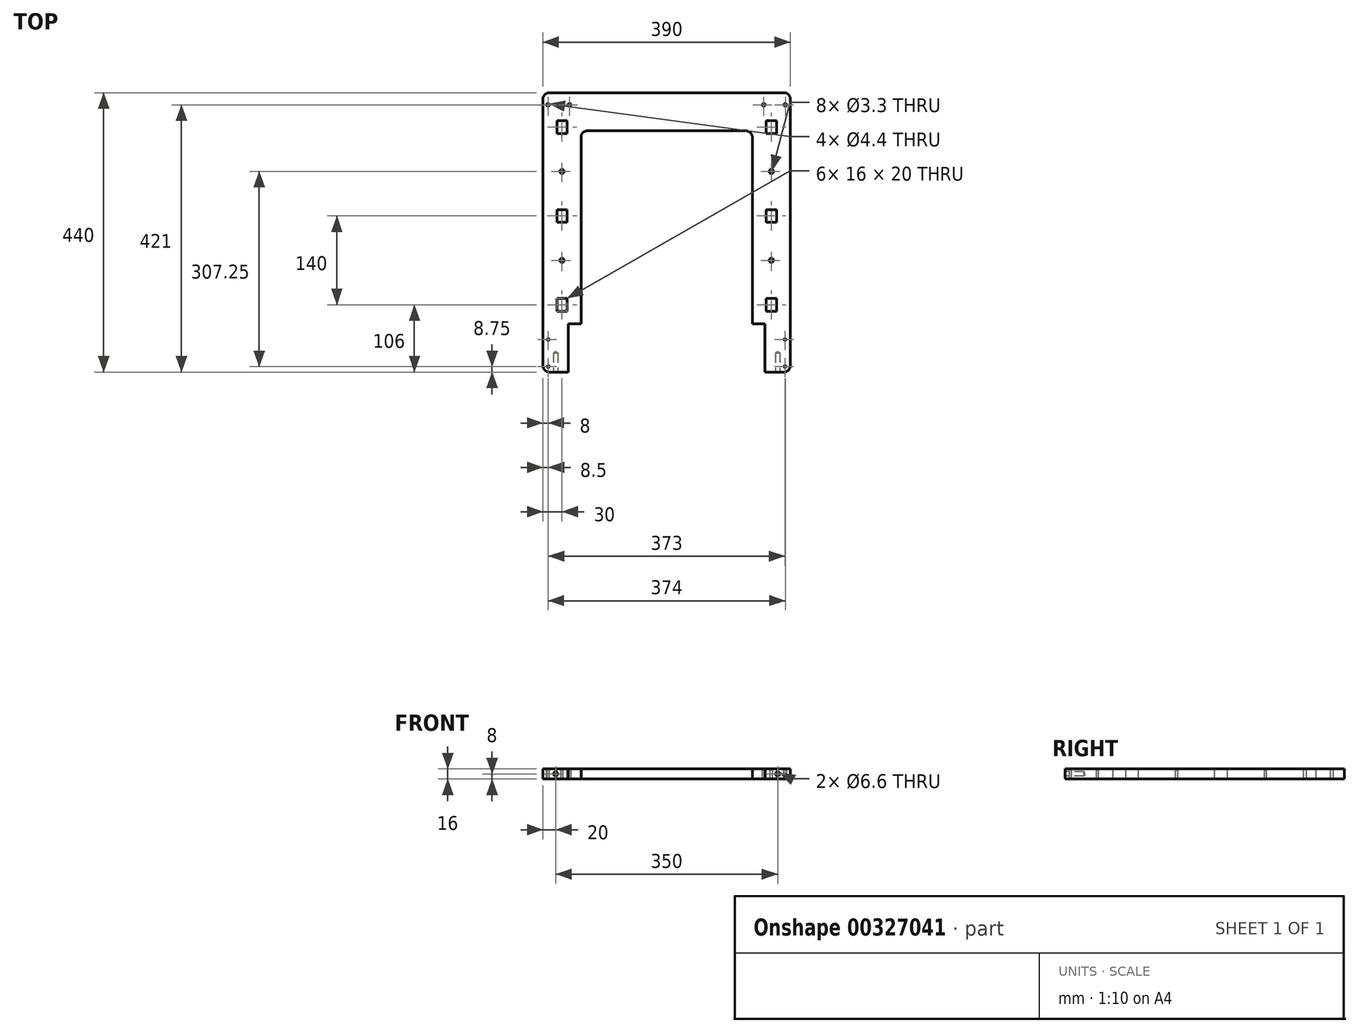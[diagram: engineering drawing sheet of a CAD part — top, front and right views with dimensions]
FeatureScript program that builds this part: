
annotation { "Feature Type Name" : "Feature", "Feature Type Description" : "" }
export const myFeature = defineFeature(function(context is Context, id is Id, definition is map)
    precondition{}
    {
        {
            var Q0;
            Q0=qCreatedBy(makeId("Top.planeOp"),FACE);
            var sketch = newSketch(context, id + "F0", { "sketchPlane" : qUnion([Q0])});
            skLineSegment(sketch, "E0.bottom", {"start": v(195, 220) * mm, "end": v(-195, 220) * mm});
            skLineSegment(sketch, "E0.top", {"start": v(195, -220) * mm, "end": v(-195, -220) * mm});
            skLineSegment(sketch, "E0.left", {"start": v(195, 220) * mm, "end": v(195, -220) * mm});
            skLineSegment(sketch, "E0.right", {"start": v(-195, 220) * mm, "end": v(-195, -220) * mm});
            skPoint(sketch, "E0.middle", {"position": v(0, 0) * mm});
            skLineSegment(sketch, "E1", {"start": v(-135, -220) * mm, "end": v(-135, 160) * mm});
            skLineSegment(sketch, "E2", {"start": v(-135, 160) * mm, "end": v(135, 160) * mm});
            skLineSegment(sketch, "E3", {"start": v(135, 160) * mm, "end": v(135, -220) * mm});
            skLineSegment(sketch, "E4", {"start": v(0, 0) * mm, "end": v(0, 160) * mm, "construction": true});
            skSolve(sketch);
        }
        {
            var Q0;
            Q0=makeQuery(id+"F0.imprint","IMPRINT",FACE,{"disambiguationData":[TD([[makeQuery(id+"F0.imprint","IMPRINT",EDGE,{"derivedFrom":sQuery(id+"F0.wireOp",EDGE,"E0.bottom")}),1.0]])]});
            extrude(context, id + "F1", {"entities" : qUnion([Q0]), "depth" : 16 * mm});
        }
        {
            var Q0;
            Q0=makeQuery(id+"F1.opExtrude","CAP_FACE",FACE,{"disambiguationData":[OSD([sQuery(id+"F0.wireOp",EDGE,"E0.bottom"),sQuery(id+"F0.wireOp",EDGE,"E0.top"),sQuery(id+"F0.wireOp",EDGE,"E0.left"),sQuery(id+"F0.wireOp",EDGE,"E0.right"),sQuery(id+"F0.wireOp",EDGE,"E1"),sQuery(id+"F0.wireOp",EDGE,"E2"),sQuery(id+"F0.wireOp",EDGE,"E3")])],"isStart":false});
            var sketch = newSketch(context, id + "F2", { "sketchPlane" : qUnion([Q0])});
            skLineSegment(sketch, "E5", {"start": v(-165, 166) * mm, "end": v(-165, 26) * mm, "construction": true});
            skLineSegment(sketch, "E6", {"start": v(-165, 26) * mm, "end": v(-165, -114) * mm, "construction": true});
            skLineSegment(sketch, "E7.bottom", {"start": v(-157, 176) * mm, "end": v(-173, 176) * mm});
            skLineSegment(sketch, "E7.top", {"start": v(-157, 156) * mm, "end": v(-173, 156) * mm});
            skLineSegment(sketch, "E7.left", {"start": v(-157, 176) * mm, "end": v(-157, 156) * mm});
            skLineSegment(sketch, "E7.right", {"start": v(-173, 176) * mm, "end": v(-173, 156) * mm});
            skPoint(sketch, "E7.middle", {"position": v(-165, 166) * mm});
            skLineSegment(sketch, "E8.bottom", {"start": v(-157, 36) * mm, "end": v(-173, 36) * mm});
            skLineSegment(sketch, "E8.top", {"start": v(-157, 16) * mm, "end": v(-173, 16) * mm});
            skLineSegment(sketch, "E8.left", {"start": v(-157, 36) * mm, "end": v(-157, 16) * mm});
            skLineSegment(sketch, "E8.right", {"start": v(-173, 36) * mm, "end": v(-173, 16) * mm});
            skPoint(sketch, "E8.middle", {"position": v(-165, 26) * mm});
            skLineSegment(sketch, "E9.bottom", {"start": v(-157, -104) * mm, "end": v(-173, -104) * mm});
            skLineSegment(sketch, "E9.top", {"start": v(-157, -124) * mm, "end": v(-173, -124) * mm});
            skLineSegment(sketch, "E9.left", {"start": v(-157, -104) * mm, "end": v(-157, -124) * mm});
            skLineSegment(sketch, "E9.right", {"start": v(-173, -104) * mm, "end": v(-173, -124) * mm});
            skPoint(sketch, "E9.middle", {"position": v(-165, -114) * mm});
            skLineSegment(sketch, "E10.MirrorCS", {"start": v(157, 36) * mm, "end": v(173, 36) * mm});
            skLineSegment(sketch, "E11.MirrorCS", {"start": v(173, 176) * mm, "end": v(173, 156) * mm});
            skLineSegment(sketch, "E12.MirrorCS", {"start": v(157, 156) * mm, "end": v(173, 156) * mm});
            skLineSegment(sketch, "E13.MirrorCS", {"start": v(157, 176) * mm, "end": v(173, 176) * mm});
            skLineSegment(sketch, "E14.MirrorCS", {"start": v(157, 16) * mm, "end": v(173, 16) * mm});
            skLineSegment(sketch, "E15.MirrorCS", {"start": v(157, 36) * mm, "end": v(157, 16) * mm});
            skLineSegment(sketch, "E16.MirrorCS", {"start": v(173, 36) * mm, "end": v(173, 16) * mm});
            skLineSegment(sketch, "E17.MirrorCS", {"start": v(157, -104) * mm, "end": v(173, -104) * mm});
            skLineSegment(sketch, "E18.MirrorCS", {"start": v(157, -124) * mm, "end": v(173, -124) * mm});
            skLineSegment(sketch, "E19.MirrorCS", {"start": v(173, -104) * mm, "end": v(173, -124) * mm});
            skLineSegment(sketch, "E20.MirrorCS", {"start": v(157, -104) * mm, "end": v(157, -124) * mm});
            skLineSegment(sketch, "E21.MirrorCS", {"start": v(157, 176) * mm, "end": v(157, 156) * mm});
            skLineSegment(sketch, "E22.MirrorCS", {"start": v(165, 166) * mm, "end": v(165, 26) * mm, "construction": true});
            skLineSegment(sketch, "E23.MirrorCS", {"start": v(165, 26) * mm, "end": v(165, -114) * mm, "construction": true});
            skPoint(sketch, "E24.MirrorP", {"position": v(165, 26) * mm});
            skPoint(sketch, "E25.MirrorP", {"position": v(165, 166) * mm});
            skPoint(sketch, "E26.MirrorP", {"position": v(165, -114) * mm});
            skLineSegment(sketch, "E27.bottom", {"start": v(-135, -220) * mm, "end": v(-155, -220) * mm});
            skLineSegment(sketch, "E27.top", {"start": v(-135, -144) * mm, "end": v(-155, -144) * mm});
            skLineSegment(sketch, "E27.left", {"start": v(-135, -220) * mm, "end": v(-135, -144) * mm});
            skLineSegment(sketch, "E27.right", {"start": v(-155, -220) * mm, "end": v(-155, -144) * mm});
            skLineSegment(sketch, "E28.MirrorCS", {"start": v(135, -144) * mm, "end": v(155, -144) * mm});
            skLineSegment(sketch, "E29.MirrorCS", {"start": v(135, -220) * mm, "end": v(155, -220) * mm});
            skLineSegment(sketch, "E30.MirrorCS", {"start": v(155, -220) * mm, "end": v(155, -144) * mm});
            skLineSegment(sketch, "E31.MirrorCS", {"start": v(135, -220) * mm, "end": v(135, -144) * mm});
            skSolve(sketch);
        }
        {
            var Q0;
            Q0=makeQuery(id+"F2.imprint","IMPRINT",FACE,{"disambiguationData":[TD([[makeQuery(id+"F2.imprint","IMPRINT",EDGE,{"derivedFrom":sQuery(id+"F2.wireOp",EDGE,"E27.bottom")}),-1.0]])]});
            var Q1;
            Q1=makeQuery(id+"F2.imprint","IMPRINT",FACE,{"disambiguationData":[TD([[makeQuery(id+"F2.imprint","IMPRINT",EDGE,{"derivedFrom":sQuery(id+"F2.wireOp",EDGE,"E7.bottom")}),1.0]])]});
            var Q2;
            Q2=makeQuery(id+"F2.imprint","IMPRINT",FACE,{"disambiguationData":[TD([[makeQuery(id+"F2.imprint","IMPRINT",EDGE,{"derivedFrom":sQuery(id+"F2.wireOp",EDGE,"E9.bottom")}),1.0]])]});
            var Q3;
            Q3=makeQuery(id+"F2.imprint","IMPRINT",FACE,{"disambiguationData":[TD([[makeQuery(id+"F2.imprint","IMPRINT",EDGE,{"derivedFrom":sQuery(id+"F2.wireOp",EDGE,"E8.bottom")}),1.0]])]});
            var Q4;
            Q4=makeQuery(id+"F2.imprint","IMPRINT",FACE,{"disambiguationData":[TD([[makeQuery(id+"F2.imprint","IMPRINT",EDGE,{"derivedFrom":sQuery(id+"F2.wireOp",EDGE,"E28.MirrorCS")}),-1.0]])]});
            var Q5;
            Q5=makeQuery(id+"F2.imprint","IMPRINT",FACE,{"disambiguationData":[TD([[makeQuery(id+"F2.imprint","IMPRINT",EDGE,{"derivedFrom":sQuery(id+"F2.wireOp",EDGE,"E10.MirrorCS")}),-1.0]])]});
            var Q6;
            Q6=makeQuery(id+"F2.imprint","IMPRINT",FACE,{"disambiguationData":[TD([[makeQuery(id+"F2.imprint","IMPRINT",EDGE,{"derivedFrom":sQuery(id+"F2.wireOp",EDGE,"E11.MirrorCS")}),-1.0]])]});
            var Q7;
            Q7=makeQuery(id+"F2.imprint","IMPRINT",FACE,{"disambiguationData":[TD([[makeQuery(id+"F2.imprint","IMPRINT",EDGE,{"derivedFrom":sQuery(id+"F2.wireOp",EDGE,"E17.MirrorCS")}),-1.0]])]});
            extrude(context, id + "F3", {"entities" : qUnion([Q0, Q1, Q2, Q3, Q4, Q5, Q6, Q7]), "operationType" : NewBodyOperationType.REMOVE, "endBound" : BoundingType.UP_TO_NEXT, "oppositeDirection" : true, "depth" : 25 * mm});
        }
        {
            var Q0;
            Q0=makeQuery(id+"F1.opExtrude","SWEPT_EDGE",EDGE,{"disambiguationData":[OSD([sQuery(id+"F0.wireOp",EDGE,"E1"),sQuery(id+"F0.wireOp",EDGE,"E2")])]});
            var Q1;
            Q1=makeQuery(id+"F1.opExtrude","SWEPT_EDGE",EDGE,{"disambiguationData":[OSD([sQuery(id+"F0.wireOp",EDGE,"E2"),sQuery(id+"F0.wireOp",EDGE,"E3")])]});
            var Q2;
            Q2=makeQuery(id+"F1.opExtrude","SWEPT_EDGE",EDGE,{"disambiguationData":[OSD([sQuery(id+"F0.wireOp",EDGE,"E0.bottom"),sQuery(id+"F0.wireOp",EDGE,"E0.right")])]});
            var Q3;
            Q3=makeQuery(id+"F1.opExtrude","SWEPT_EDGE",EDGE,{"disambiguationData":[OSD([sQuery(id+"F0.wireOp",EDGE,"E0.bottom"),sQuery(id+"F0.wireOp",EDGE,"E0.left")])]});
            var Q4;
            Q4=makeQuery(id+"F1.opExtrude","SWEPT_EDGE",EDGE,{"disambiguationData":[OSD([sQuery(id+"F0.wireOp",EDGE,"E0.top"),sQuery(id+"F0.wireOp",EDGE,"E0.left")])]});
            var Q5;
            Q5=makeQuery(id+"F3.boolean.opBoolean","COPY",EDGE,{"derivedFrom":makeQuery(id+"F3.opExtrude","SWEPT_EDGE",EDGE,{"disambiguationData":[OSD([sQuery(id+"F0.wireOp",EDGE,"E0.top"),sQuery(id+"F2.wireOp",EDGE,"E29.MirrorCS"),sQuery(id+"F2.wireOp",EDGE,"E30.MirrorCS")])]})});
            var Q6;
            Q6=makeQuery(id+"F3.boolean.opBoolean","COPY",EDGE,{"derivedFrom":makeQuery(id+"F3.opExtrude","SWEPT_EDGE",EDGE,{"disambiguationData":[OSD([sQuery(id+"F0.wireOp",EDGE,"E0.top"),sQuery(id+"F2.wireOp",EDGE,"E27.bottom"),sQuery(id+"F2.wireOp",EDGE,"E27.right")])]})});
            var Q7;
            Q7=makeQuery(id+"F1.opExtrude","SWEPT_EDGE",EDGE,{"disambiguationData":[OSD([sQuery(id+"F0.wireOp",EDGE,"E0.top"),sQuery(id+"F0.wireOp",EDGE,"E0.right")])]});
            fillet(context, id + "F4", {"entities" : qUnion([Q0, Q1, Q2, Q3, Q4, Q5, Q6, Q7]), "radius" : 10 * mm, "tangentPropagation" : true, "allowEdgeOverflow" : false});
        }
        {
            var Q0;
            Q0=makeQuery(id+"F1.opExtrude","CAP_FACE",FACE,{"disambiguationData":[OSD([sQuery(id+"F0.wireOp",EDGE,"E0.bottom"),sQuery(id+"F0.wireOp",EDGE,"E0.top"),sQuery(id+"F0.wireOp",EDGE,"E0.left"),sQuery(id+"F0.wireOp",EDGE,"E0.right"),sQuery(id+"F0.wireOp",EDGE,"E1"),sQuery(id+"F0.wireOp",EDGE,"E2"),sQuery(id+"F0.wireOp",EDGE,"E3")])],"isStart":false});
            var sketch = newSketch(context, id + "F5", { "sketchPlane" : qUnion([Q0])});
            skLineSegment(sketch, "E32", {"start": v(-165, 36) * mm, "end": v(-165, 96) * mm});
            skLineSegment(sketch, "E33", {"start": v(-165, 16) * mm, "end": v(-165, -44) * mm});
            skLineSegment(sketch, "E34", {"start": v(165, 36) * mm, "end": v(165, 96) * mm});
            skLineSegment(sketch, "E35", {"start": v(165, 16) * mm, "end": v(165, -44) * mm});
            skSolve(sketch);
        }
        {
            var Q0;
            Q0=sQuery(id+"F5.wireOp",VERTEX,"E32.end");
            var Q1;
            Q1=sQuery(id+"F5.wireOp",VERTEX,"E33.end");
            var Q2;
            Q2=sQuery(id+"F5.wireOp",VERTEX,"E34.end");
            var Q3;
            Q3=sQuery(id+"F5.wireOp",VERTEX,"E35.end");
            var Q4;
            Q4=makeQuery(id+"F1.opExtrude","SWEPT_BODY",BODY,{"disambiguationData":[OSD([sQuery(id+"F0.wireOp",EDGE,"E0.bottom"),sQuery(id+"F0.wireOp",EDGE,"E0.top"),sQuery(id+"F0.wireOp",EDGE,"E0.left"),sQuery(id+"F0.wireOp",EDGE,"E0.right"),sQuery(id+"F0.wireOp",EDGE,"E1"),sQuery(id+"F0.wireOp",EDGE,"E2"),sQuery(id+"F0.wireOp",EDGE,"E3")])]});
            hole(context, id + "F6", {"style" : HoleStyle.C_SINK, "endStyle" : HoleEndStyle.THROUGH, "standardTappedOrClearance" : lookupTablePath({ "standard" : "ISO", "fit" : "Normal", "size" : "M3", "type" : "Clearance" }), "standardBlindInLast" : lookupTablePath({ "fit" : "Standard", "standard" : "ISO", "size" : "M3", "type" : "Clearance" }), "holeDiameter" : 3.3 * mm, "cSinkDiameter" : 6.72 * mm, "cSinkAngle" : 90 * degree, "tappedDepth" : 12 * mm, "tapClearance" : 3, "locations" : qUnion([Q0, Q1, Q2, Q3]), "scope" : qUnion([Q4])});
        }
        {
            var Q0;
            {var subQ0=sQuery(id+"F0.wireOp",EDGE,"E0.top");Q0=makeQuery(id+"F1.opExtrude","SWEPT_FACE",FACE,{"disambiguationData":[OSD([subQ0]),TDD([makeQuery(id+"F0.imprint","IMPRINT",EDGE,{"disambiguationData":[TD([[makeQuery(id+"F0.imprint","INTERSECT",VERTEX,{"derivedFrom":[subQ0,sQuery(id+"F0.wireOp",EDGE,"E0.right")]}),1.0]])],"derivedFrom":subQ0})])]});}
            var sketch = newSketch(context, id + "F7", { "sketchPlane" : qUnion([Q0])});
            skLineSegment(sketch, "E36", {"start": v(-165, 0) * mm, "end": v(-175, 8) * mm});
            skLineSegment(sketch, "E37", {"start": v(-175, 8) * mm, "end": v(-185, 16) * mm});
            skLineSegment(sketch, "E38.0.0", {"start": v(185, 16) * mm, "end": v(165, 16) * mm});
            skLineSegment(sketch, "E38.0.1", {"start": v(165, 16) * mm, "end": v(165, 0) * mm});
            skLineSegment(sketch, "E38.0.2", {"start": v(165, 0) * mm, "end": v(185, 0) * mm});
            skLineSegment(sketch, "E38.0.3", {"start": v(185, 0) * mm, "end": v(185, 16) * mm});
            skLineSegment(sketch, "E39", {"start": v(185, 0) * mm, "end": v(175, 8) * mm});
            skPoint(sketch, "E39.endSnap0", {"position": v(165, 8) * mm});
            skPoint(sketch, "E39.endSnap1", {"position": v(175, 16) * mm});
            skLineSegment(sketch, "E40", {"start": v(175, 8) * mm, "end": v(165, 16) * mm});
            skSolve(sketch);
        }
        {
            var Q0;
            Q0=sQuery(id+"F7.wireOp",VERTEX,"E37.start");
            var Q1;
            Q1=sQuery(id+"F7.wireOp",VERTEX,"E40.start");
            var Q2;
            Q2=makeQuery(id+"F1.opExtrude","SWEPT_BODY",BODY,{"disambiguationData":[OSD([sQuery(id+"F0.wireOp",EDGE,"E0.bottom"),sQuery(id+"F0.wireOp",EDGE,"E0.top"),sQuery(id+"F0.wireOp",EDGE,"E0.left"),sQuery(id+"F0.wireOp",EDGE,"E0.right"),sQuery(id+"F0.wireOp",EDGE,"E1"),sQuery(id+"F0.wireOp",EDGE,"E2"),sQuery(id+"F0.wireOp",EDGE,"E3")])]});
            hole(context, id + "F8", {"style" : HoleStyle.SIMPLE, "endStyle" : HoleEndStyle.BLIND, "standardTappedOrClearance" : lookupTablePath({ "standard" : "ISO", "fit" : "Normal", "size" : "M6", "type" : "Clearance" }), "standardBlindInLast" : lookupTablePath({ "fit" : "Standard", "standard" : "ISO", "size" : "M6", "type" : "Clearance" }), "holeDiameter" : 6.6 * mm, "holeDepth" : 30 * mm, "tappedDepth" : 12 * mm, "tapClearance" : 3, "locations" : qUnion([Q0, Q1]), "scope" : qUnion([Q2])});
        }
        {
            var Q0;
            Q0=makeQuery(id+"F1.opExtrude","CAP_FACE",FACE,{"disambiguationData":[OSD([sQuery(id+"F0.wireOp",EDGE,"E0.bottom"),sQuery(id+"F0.wireOp",EDGE,"E0.top"),sQuery(id+"F0.wireOp",EDGE,"E0.left"),sQuery(id+"F0.wireOp",EDGE,"E0.right"),sQuery(id+"F0.wireOp",EDGE,"E1"),sQuery(id+"F0.wireOp",EDGE,"E2"),sQuery(id+"F0.wireOp",EDGE,"E3")])],"isStart":false});
            var sketch = newSketch(context, id + "F9", { "sketchPlane" : qUnion([Q0])});
            skLineSegment(sketch, "E41", {"start": v(-195, 201) * mm, "end": v(-187, 201) * mm});
            skLineSegment(sketch, "E42", {"start": v(-187, 201) * mm, "end": v(-153, 201) * mm});
            skLineSegment(sketch, "E43.MirrorCS", {"start": v(195, 201) * mm, "end": v(187, 201) * mm});
            skLineSegment(sketch, "E44.MirrorCS", {"start": v(187, 201) * mm, "end": v(153, 201) * mm});
            skSolve(sketch);
        }
        {
            var Q0;
            Q0=sQuery(id+"F9.wireOp",VERTEX,"E42.start");
            var Q1;
            Q1=sQuery(id+"F9.wireOp",VERTEX,"E42.end");
            var Q2;
            Q2=sQuery(id+"F9.wireOp",VERTEX,"E44.MirrorCS.start");
            var Q3;
            Q3=sQuery(id+"F9.wireOp",VERTEX,"E44.MirrorCS.end");
            var Q4;
            Q4=makeQuery(id+"F1.opExtrude","SWEPT_BODY",BODY,{"disambiguationData":[OSD([sQuery(id+"F0.wireOp",EDGE,"E0.bottom"),sQuery(id+"F0.wireOp",EDGE,"E0.top"),sQuery(id+"F0.wireOp",EDGE,"E0.left"),sQuery(id+"F0.wireOp",EDGE,"E0.right"),sQuery(id+"F0.wireOp",EDGE,"E1"),sQuery(id+"F0.wireOp",EDGE,"E2"),sQuery(id+"F0.wireOp",EDGE,"E3")])]});
            hole(context, id + "F10", {"style" : HoleStyle.SIMPLE, "endStyle" : HoleEndStyle.THROUGH, "standardTappedOrClearance" : lookupTablePath({ "standard" : "ISO", "fit" : "Normal", "size" : "M4", "type" : "Clearance" }), "standardBlindInLast" : lookupTablePath({ "fit" : "Standard", "standard" : "ISO", "size" : "M4", "type" : "Clearance" }), "holeDiameter" : 4.4 * mm, "tappedDepth" : 12 * mm, "tapClearance" : 3, "locations" : qUnion([Q0, Q1, Q2, Q3]), "scope" : qUnion([Q4])});
        }
        {
            var Q0;
            Q0=makeQuery(id+"F1.opExtrude","CAP_FACE",FACE,{"disambiguationData":[OSD([sQuery(id+"F0.wireOp",EDGE,"E0.bottom"),sQuery(id+"F0.wireOp",EDGE,"E0.top"),sQuery(id+"F0.wireOp",EDGE,"E0.left"),sQuery(id+"F0.wireOp",EDGE,"E0.right"),sQuery(id+"F0.wireOp",EDGE,"E1"),sQuery(id+"F0.wireOp",EDGE,"E2"),sQuery(id+"F0.wireOp",EDGE,"E3")])],"isStart":false});
            var sketch = newSketch(context, id + "F11", { "sketchPlane" : qUnion([Q0])});
            skLineSegment(sketch, "E45", {"start": v(-186.5, -220) * mm, "end": v(-186.5, -211.25) * mm});
            skLineSegment(sketch, "E46", {"start": v(-186.5, -211.25) * mm, "end": v(-186.5, -168.75) * mm});
            skLineSegment(sketch, "E47.MirrorCS", {"start": v(186.5, -220) * mm, "end": v(186.5, -211.25) * mm});
            skLineSegment(sketch, "E48.MirrorCS", {"start": v(186.5, -211.25) * mm, "end": v(186.5, -168.75) * mm});
            skSolve(sketch);
        }
        {
            var Q0;
            Q0=sQuery(id+"F11.wireOp",VERTEX,"E46.end");
            var Q1;
            Q1=sQuery(id+"F11.wireOp",VERTEX,"E46.start");
            var Q2;
            Q2=sQuery(id+"F11.wireOp",VERTEX,"E48.MirrorCS.start");
            var Q3;
            Q3=sQuery(id+"F11.wireOp",VERTEX,"E48.MirrorCS.end");
            var Q4;
            Q4=makeQuery(id+"F1.opExtrude","SWEPT_BODY",BODY,{"disambiguationData":[OSD([sQuery(id+"F0.wireOp",EDGE,"E0.bottom"),sQuery(id+"F0.wireOp",EDGE,"E0.top"),sQuery(id+"F0.wireOp",EDGE,"E0.left"),sQuery(id+"F0.wireOp",EDGE,"E0.right"),sQuery(id+"F0.wireOp",EDGE,"E1"),sQuery(id+"F0.wireOp",EDGE,"E2"),sQuery(id+"F0.wireOp",EDGE,"E3")])]});
            hole(context, id + "F12", {"style" : HoleStyle.SIMPLE, "endStyle" : HoleEndStyle.THROUGH, "standardTappedOrClearance" : lookupTablePath({ "standard" : "ISO", "fit" : "Normal", "size" : "M3", "type" : "Clearance" }), "standardBlindInLast" : lookupTablePath({ "fit" : "Standard", "standard" : "ISO", "size" : "M3", "type" : "Clearance" }), "holeDiameter" : 3.3 * mm, "tappedDepth" : 12 * mm, "tapClearance" : 3, "locations" : qUnion([Q0, Q1, Q2, Q3]), "scope" : qUnion([Q4])});
        }
    });
